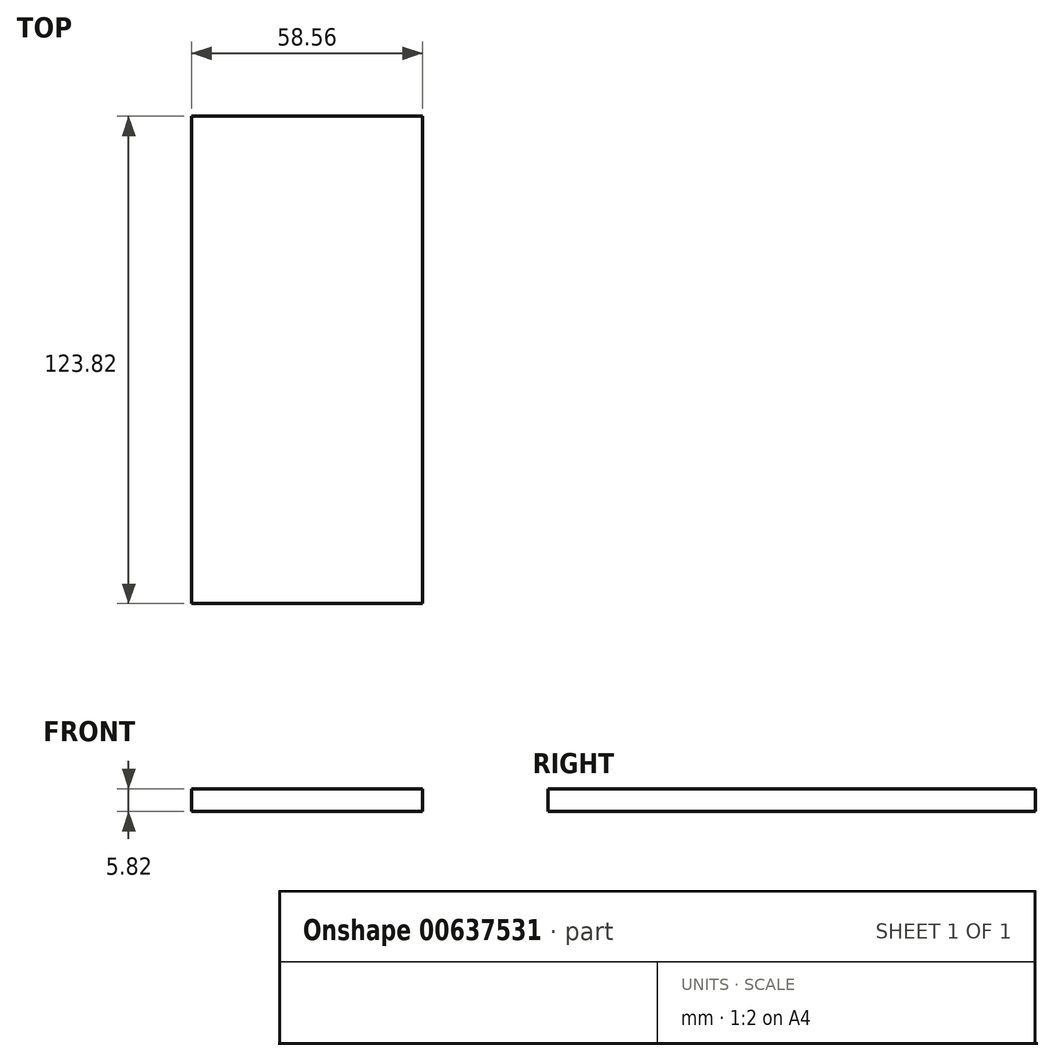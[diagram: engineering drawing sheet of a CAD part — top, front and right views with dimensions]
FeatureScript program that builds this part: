
annotation { "Feature Type Name" : "Feature", "Feature Type Description" : "" }
export const myFeature = defineFeature(function(context is Context, id is Id, definition is map)
    precondition{}
    {
        {
            var Q0;
            Q0=qCreatedBy(makeId("Top.planeOp"),FACE);
            var sketch = newSketch(context, id + "F0", { "sketchPlane" : qUnion([Q0])});
            skLineSegment(sketch, "E0.bottom", {"start": v(-29.28, 61.91) * mm, "end": v(29.28, 61.91) * mm});
            skLineSegment(sketch, "E0.top", {"start": v(-29.28, -61.91) * mm, "end": v(29.28, -61.91) * mm});
            skLineSegment(sketch, "E0.left", {"start": v(-29.28, 61.91) * mm, "end": v(-29.28, -61.91) * mm});
            skLineSegment(sketch, "E0.right", {"start": v(29.28, 61.91) * mm, "end": v(29.28, -61.91) * mm});
            skPoint(sketch, "E0.middle", {"position": v(0, 0) * mm});
            skSolve(sketch);
        }
        {
            var Q0;
            Q0=makeQuery(id+"F0.imprint","IMPRINT",FACE,{"disambiguationData":[TD([[makeQuery(id+"F0.imprint","IMPRINT",EDGE,{"derivedFrom":sQuery(id+"F0.wireOp",EDGE,"E0.bottom")}),-1.0]])]});
            extrude(context, id + "F1", {"entities" : qUnion([Q0]), "depth" : 5.82 * mm, "offsetDistance" : 25.4 * mm});
        }
    });
